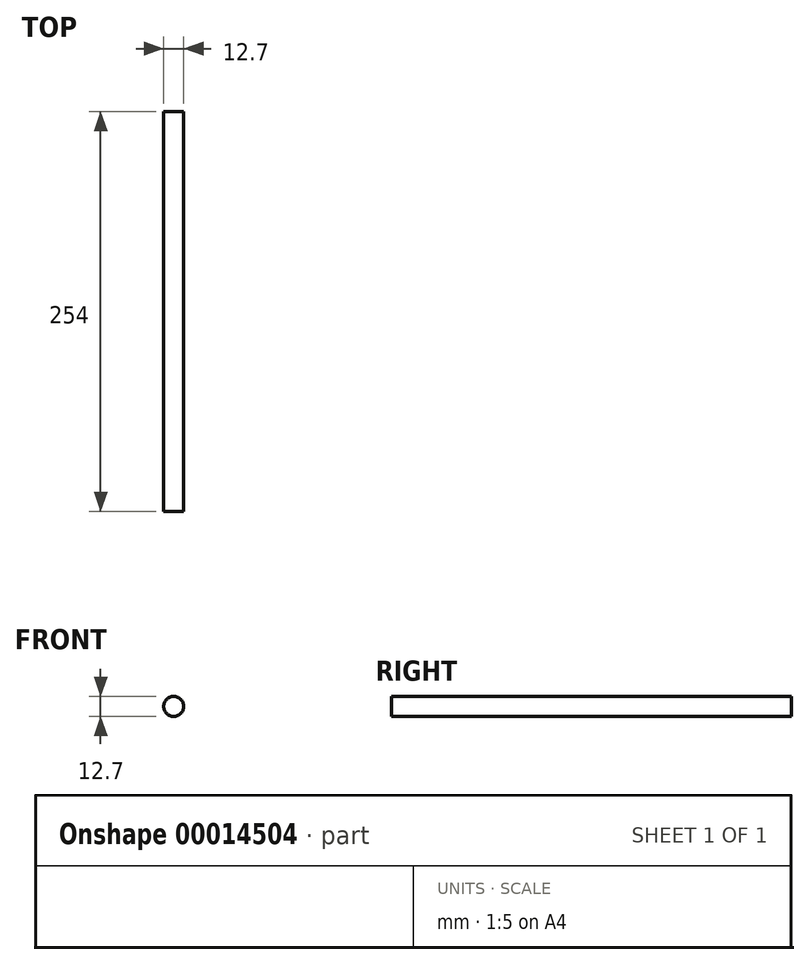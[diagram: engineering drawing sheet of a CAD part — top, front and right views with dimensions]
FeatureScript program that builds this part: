
annotation { "Feature Type Name" : "Feature", "Feature Type Description" : "" }
export const myFeature = defineFeature(function(context is Context, id is Id, definition is map)
    precondition{}
    {
        {
            var Q0;
            Q0=qCreatedBy(makeId("Front.planeOp"),FACE);
            var sketch = newSketch(context, id + "F0", { "sketchPlane" : qUnion([Q0])});
            skCircle(sketch, "E0", {"center": v(0, 0) * mm, "radius": 6.35 * mm});
            skSolve(sketch);
        }
        {
            var Q0;
            Q0 = qSketchRegion(id + "F0", true);
            extrude(context, id + "F1", {"entities" : qUnion([Q0]), "depth" : 254 * mm, "symmetric" : true});
        }
    });
